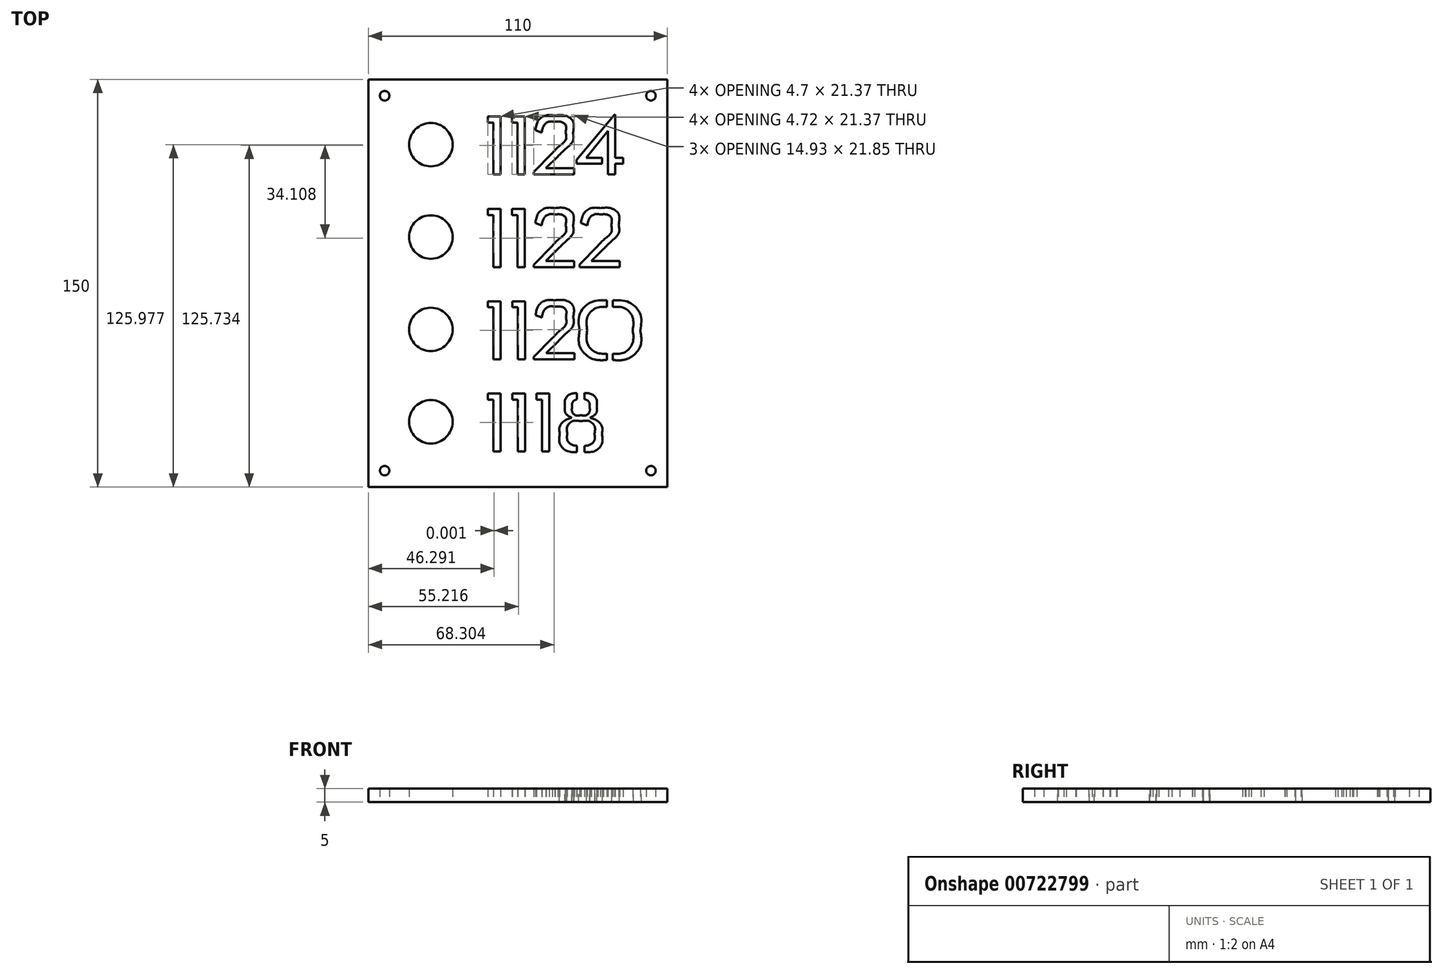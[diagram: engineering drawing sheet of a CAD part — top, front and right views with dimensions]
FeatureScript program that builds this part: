
annotation { "Feature Type Name" : "Feature", "Feature Type Description" : "" }
export const myFeature = defineFeature(function(context is Context, id is Id, definition is map)
    precondition{}
    {
        {
            var Q0;
            Q0=qCreatedBy(makeId("Top.planeOp"),FACE);
            var sketch = newSketch(context, id + "F0", { "sketchPlane" : qUnion([Q0])});
            skLineSegment(sketch, "E0.bottom", {"start": v(-57.93, 74.31) * mm, "end": v(52.07, 74.31) * mm});
            skLineSegment(sketch, "E0.top", {"start": v(-57.93, -75.69) * mm, "end": v(52.07, -75.69) * mm});
            skLineSegment(sketch, "E0.left", {"start": v(-57.93, 74.31) * mm, "end": v(-57.93, -75.69) * mm});
            skLineSegment(sketch, "E0.right", {"start": v(52.07, 74.31) * mm, "end": v(52.07, -75.69) * mm});
            skCircle(sketch, "E1", {"center": v(-51.93, 68.31) * mm, "radius": 1.75 * mm});
            skLineSegment(sketch, "E2.bottom", {"start": v(-57.93, 74.31) * mm, "end": v(-41.03, 74.31) * mm});
            skLineSegment(sketch, "E2.left", {"start": v(-57.93, 74.31) * mm, "end": v(-57.93, 53.12) * mm});
            skLineSegment(sketch, "E3.left", {"start": v(52.07, 74.31) * mm, "end": v(52.07, 53.12) * mm});
            skCircle(sketch, "E4", {"center": v(46.07, 68.31) * mm, "radius": 1.75 * mm});
            skCircle(sketch, "E5", {"center": v(-51.93, -69.69) * mm, "radius": 1.75 * mm});
            skCircle(sketch, "E6", {"center": v(46.07, -69.69) * mm, "radius": 1.75 * mm});
            skCircle(sketch, "E7", {"center": v(-34.93, 50.31) * mm, "radius": 8 * mm});
            skCircle(sketch, "E8", {"center": v(-34.93, 16.31) * mm, "radius": 8 * mm});
            skCircle(sketch, "E9", {"center": v(-34.93, -17.69) * mm, "radius": 8 * mm});
            skCircle(sketch, "E10", {"center": v(-34.93, -51.69) * mm, "radius": 8 * mm});
            skLineSegment(sketch, "E11", {"start": v(-13.99, 24.37) * mm, "end": v(-11.95, 24.37) * mm});
            skLineSegment(sketch, "E12", {"start": v(-11.95, 24.37) * mm, "end": v(-11.95, 5.25) * mm});
            skLineSegment(sketch, "E13", {"start": v(-11.95, 5.25) * mm, "end": v(-9.29, 5.25) * mm});
            skLineSegment(sketch, "E14", {"start": v(-9.29, 5.25) * mm, "end": v(-9.29, 26.62) * mm});
            skLineSegment(sketch, "E15", {"start": v(-9.29, 26.62) * mm, "end": v(-13.99, 26.62) * mm});
            skLineSegment(sketch, "E16", {"start": v(-13.99, 26.62) * mm, "end": v(-13.99, 24.37) * mm});
            skLineSegment(sketch, "E17", {"start": v(-5.07, 24.37) * mm, "end": v(-3.02, 24.37) * mm});
            skLineSegment(sketch, "E18", {"start": v(-3.02, 24.37) * mm, "end": v(-3.02, 5.25) * mm});
            skLineSegment(sketch, "E19", {"start": v(-3.02, 5.25) * mm, "end": v(-0.35, 5.25) * mm});
            skLineSegment(sketch, "E20", {"start": v(-0.35, 5.25) * mm, "end": v(-0.35, 26.62) * mm});
            skLineSegment(sketch, "E21", {"start": v(-0.35, 26.62) * mm, "end": v(-5.07, 26.62) * mm});
            skLineSegment(sketch, "E22", {"start": v(-5.07, 26.62) * mm, "end": v(-5.07, 24.37) * mm});
            skLineSegment(sketch, "E23", {"start": v(24.17, 7.5) * mm, "end": v(28.58, 11.87) * mm});
            skLineSegment(sketch, "E24", {"start": v(20.3, 21.5) * mm, "end": v(22.63, 20.62) * mm});
            skLineSegment(sketch, "E25", {"start": v(26.54, 13.08) * mm, "end": v(19.84, 6.27) * mm});
            skLineSegment(sketch, "E26", {"start": v(19.84, 6.27) * mm, "end": v(19.84, 5.25) * mm});
            skLineSegment(sketch, "E27", {"start": v(19.84, 5.25) * mm, "end": v(34.62, 5.25) * mm});
            skLineSegment(sketch, "E28", {"start": v(34.62, 5.25) * mm, "end": v(34.62, 7.5) * mm});
            skLineSegment(sketch, "E29", {"start": v(34.62, 7.5) * mm, "end": v(24.17, 7.5) * mm});
            skLineSegment(sketch, "E30", {"start": v(3.51, 21.5) * mm, "end": v(5.84, 20.62) * mm});
            skLineSegment(sketch, "E31", {"start": v(9.76, 13.08) * mm, "end": v(2.9, 6.12) * mm});
            skLineSegment(sketch, "E32", {"start": v(2.9, 6.12) * mm, "end": v(2.9, 5.25) * mm});
            skLineSegment(sketch, "E33", {"start": v(2.9, 5.25) * mm, "end": v(17.84, 5.25) * mm});
            skLineSegment(sketch, "E34", {"start": v(17.84, 5.25) * mm, "end": v(17.84, 7.5) * mm});
            skLineSegment(sketch, "E35", {"start": v(17.84, 7.5) * mm, "end": v(7.39, 7.5) * mm});
            skLineSegment(sketch, "E36", {"start": v(7.39, 7.5) * mm, "end": v(11.8, 11.88) * mm});
            skLineSegment(sketch, "E37", {"start": v(-13.9, -9.56) * mm, "end": v(-11.87, -9.56) * mm});
            skLineSegment(sketch, "E38", {"start": v(-11.87, -9.56) * mm, "end": v(-11.87, -28.68) * mm});
            skLineSegment(sketch, "E39", {"start": v(-11.87, -28.68) * mm, "end": v(-9.2, -28.68) * mm});
            skLineSegment(sketch, "E40", {"start": v(-9.2, -28.68) * mm, "end": v(-9.2, -7.31) * mm});
            skLineSegment(sketch, "E41", {"start": v(-9.2, -7.31) * mm, "end": v(-13.9, -7.31) * mm});
            skLineSegment(sketch, "E42", {"start": v(-13.9, -7.31) * mm, "end": v(-13.9, -9.56) * mm});
            skLineSegment(sketch, "E43", {"start": v(3.6, -12.44) * mm, "end": v(5.93, -13.31) * mm});
            skLineSegment(sketch, "E44", {"start": v(9.84, -20.85) * mm, "end": v(3, -27.81) * mm});
            skLineSegment(sketch, "E45", {"start": v(3, -27.81) * mm, "end": v(3, -28.68) * mm});
            skLineSegment(sketch, "E46", {"start": v(3, -28.68) * mm, "end": v(17.92, -28.68) * mm});
            skLineSegment(sketch, "E47", {"start": v(17.92, -28.68) * mm, "end": v(17.92, -26.43) * mm});
            skLineSegment(sketch, "E48", {"start": v(17.92, -26.43) * mm, "end": v(7.47, -26.43) * mm});
            skLineSegment(sketch, "E49", {"start": v(7.47, -26.43) * mm, "end": v(11.88, -22.06) * mm});
            skLineSegment(sketch, "E50", {"start": v(-4.99, -9.56) * mm, "end": v(-2.94, -9.56) * mm});
            skLineSegment(sketch, "E51", {"start": v(-2.94, -9.56) * mm, "end": v(-2.94, -28.68) * mm});
            skLineSegment(sketch, "E52", {"start": v(-2.94, -28.68) * mm, "end": v(-0.27, -28.68) * mm});
            skLineSegment(sketch, "E53", {"start": v(-0.27, -28.68) * mm, "end": v(-0.27, -7.31) * mm});
            skLineSegment(sketch, "E54", {"start": v(-0.27, -7.31) * mm, "end": v(-4.99, -7.31) * mm});
            skLineSegment(sketch, "E55", {"start": v(-4.99, -7.31) * mm, "end": v(-4.99, -9.56) * mm});
            skLineSegment(sketch, "E56", {"start": v(32.01, -7.03) * mm, "end": v(32.01, -9.38) * mm});
            skLineSegment(sketch, "E57", {"start": v(32.01, -26.62) * mm, "end": v(32.01, -28.96) * mm});
            skLineSegment(sketch, "E58", {"start": v(29.82, -9.4) * mm, "end": v(29.82, -7.04) * mm});
            skLineSegment(sketch, "E59", {"start": v(29.82, -28.96) * mm, "end": v(29.82, -26.6) * mm});
            skLineSegment(sketch, "E60", {"start": v(-13.99, 58.48) * mm, "end": v(-11.95, 58.48) * mm});
            skLineSegment(sketch, "E61", {"start": v(-11.95, 58.48) * mm, "end": v(-11.95, 39.36) * mm});
            skLineSegment(sketch, "E62", {"start": v(-11.95, 39.36) * mm, "end": v(-9.29, 39.36) * mm});
            skLineSegment(sketch, "E63", {"start": v(-9.29, 39.36) * mm, "end": v(-9.29, 60.73) * mm});
            skLineSegment(sketch, "E64", {"start": v(-9.29, 60.73) * mm, "end": v(-13.99, 60.73) * mm});
            skLineSegment(sketch, "E65", {"start": v(-13.99, 60.73) * mm, "end": v(-13.99, 58.48) * mm});
            skLineSegment(sketch, "E66", {"start": v(-5.07, 58.48) * mm, "end": v(-3.02, 58.48) * mm});
            skLineSegment(sketch, "E67", {"start": v(-3.02, 58.48) * mm, "end": v(-3.02, 39.36) * mm});
            skLineSegment(sketch, "E68", {"start": v(-3.02, 39.36) * mm, "end": v(-0.36, 39.36) * mm});
            skLineSegment(sketch, "E69", {"start": v(-0.36, 39.36) * mm, "end": v(-0.36, 60.73) * mm});
            skLineSegment(sketch, "E70", {"start": v(-0.36, 60.73) * mm, "end": v(-5.07, 60.73) * mm});
            skLineSegment(sketch, "E71", {"start": v(-5.07, 60.73) * mm, "end": v(-5.07, 58.48) * mm});
            skLineSegment(sketch, "E72", {"start": v(32.92, 45.52) * mm, "end": v(32.92, 61.35) * mm});
            skLineSegment(sketch, "E73", {"start": v(32.92, 61.35) * mm, "end": v(32.7, 61.35) * mm});
            skLineSegment(sketch, "E74", {"start": v(32.7, 61.35) * mm, "end": v(18.71, 44.73) * mm});
            skLineSegment(sketch, "E75", {"start": v(18.71, 44.73) * mm, "end": v(18.71, 43.32) * mm});
            skLineSegment(sketch, "E76", {"start": v(18.71, 43.32) * mm, "end": v(28.13, 43.32) * mm});
            skLineSegment(sketch, "E77", {"start": v(28.13, 43.32) * mm, "end": v(28.13, 45.52) * mm});
            skLineSegment(sketch, "E78", {"start": v(28.13, 45.52) * mm, "end": v(22.3, 45.52) * mm});
            skLineSegment(sketch, "E79", {"start": v(22.3, 45.52) * mm, "end": v(30.3, 55.31) * mm});
            skLineSegment(sketch, "E80", {"start": v(30.3, 55.31) * mm, "end": v(30.3, 39.36) * mm});
            skLineSegment(sketch, "E81", {"start": v(30.3, 39.36) * mm, "end": v(32.92, 39.36) * mm});
            skLineSegment(sketch, "E82", {"start": v(32.92, 39.36) * mm, "end": v(32.92, 43.32) * mm});
            skLineSegment(sketch, "E83", {"start": v(32.92, 43.32) * mm, "end": v(35.8, 43.32) * mm});
            skLineSegment(sketch, "E84", {"start": v(35.8, 43.32) * mm, "end": v(35.8, 45.52) * mm});
            skLineSegment(sketch, "E85", {"start": v(35.8, 45.52) * mm, "end": v(32.92, 45.52) * mm});
            skLineSegment(sketch, "E86", {"start": v(3.51, 55.6) * mm, "end": v(5.84, 54.73) * mm});
            skLineSegment(sketch, "E87", {"start": v(9.76, 47.2) * mm, "end": v(2.9, 40.23) * mm});
            skLineSegment(sketch, "E88", {"start": v(2.9, 40.23) * mm, "end": v(2.9, 39.36) * mm});
            skLineSegment(sketch, "E89", {"start": v(2.9, 39.36) * mm, "end": v(17.84, 39.36) * mm});
            skLineSegment(sketch, "E90", {"start": v(17.84, 39.36) * mm, "end": v(17.84, 41.6) * mm});
            skLineSegment(sketch, "E91", {"start": v(17.84, 41.6) * mm, "end": v(7.38, 41.6) * mm});
            skLineSegment(sketch, "E92", {"start": v(7.38, 41.6) * mm, "end": v(11.8, 45.98) * mm});
            skLineSegment(sketch, "E93", {"start": v(-13.92, -43.54) * mm, "end": v(-11.89, -43.54) * mm});
            skLineSegment(sketch, "E94", {"start": v(-11.89, -43.54) * mm, "end": v(-11.89, -62.66) * mm});
            skLineSegment(sketch, "E95", {"start": v(-11.89, -62.66) * mm, "end": v(-9.22, -62.66) * mm});
            skLineSegment(sketch, "E96", {"start": v(-9.22, -62.66) * mm, "end": v(-9.22, -41.29) * mm});
            skLineSegment(sketch, "E97", {"start": v(-9.22, -41.29) * mm, "end": v(-13.92, -41.29) * mm});
            skLineSegment(sketch, "E98", {"start": v(-13.92, -41.29) * mm, "end": v(-13.92, -43.54) * mm});
            skLineSegment(sketch, "E99", {"start": v(-5, -43.54) * mm, "end": v(-2.95, -43.54) * mm});
            skLineSegment(sketch, "E100", {"start": v(-2.95, -43.54) * mm, "end": v(-2.95, -62.66) * mm});
            skLineSegment(sketch, "E101", {"start": v(-2.95, -62.66) * mm, "end": v(-0.29, -62.66) * mm});
            skLineSegment(sketch, "E102", {"start": v(-0.29, -62.66) * mm, "end": v(-0.29, -41.29) * mm});
            skLineSegment(sketch, "E103", {"start": v(-0.29, -41.29) * mm, "end": v(-5, -41.29) * mm});
            skLineSegment(sketch, "E104", {"start": v(-5, -41.29) * mm, "end": v(-5, -43.54) * mm});
            skLineSegment(sketch, "E105", {"start": v(21.62, -41.08) * mm, "end": v(21.62, -43.4) * mm});
            skLineSegment(sketch, "E106", {"start": v(18.86, -43.44) * mm, "end": v(18.86, -41.1) * mm});
            skLineSegment(sketch, "E107", {"start": v(18.86, -62.89) * mm, "end": v(18.86, -60.53) * mm});
            skLineSegment(sketch, "E108", {"start": v(21.62, -60.55) * mm, "end": v(21.62, -62.9) * mm});
            skLineSegment(sketch, "E109", {"start": v(3.91, -43.54) * mm, "end": v(5.98, -43.54) * mm});
            skLineSegment(sketch, "E110", {"start": v(5.98, -43.54) * mm, "end": v(5.98, -62.66) * mm});
            skLineSegment(sketch, "E111", {"start": v(5.98, -62.66) * mm, "end": v(8.65, -62.66) * mm});
            skLineSegment(sketch, "E112", {"start": v(8.65, -62.66) * mm, "end": v(8.65, -41.29) * mm});
            skLineSegment(sketch, "E113", {"start": v(8.65, -41.29) * mm, "end": v(3.91, -41.29) * mm});
            skLineSegment(sketch, "E114", {"start": v(3.91, -41.29) * mm, "end": v(3.91, -43.54) * mm});
            skFitSpline(sketch, "E115", {"points": [v(28.58, 11.87) * mm, v(31.3, 14.54) * mm, v(34.16, 17.66) * mm, v(34.16, 20.75) * mm]});
            skFitSpline(sketch, "E116", {"points": [v(34.16, 20.75) * mm, v(34.16, 24.79) * mm, v(31.17, 26.95) * mm, v(27.46, 26.95) * mm]});
            skFitSpline(sketch, "E117", {"points": [v(27.46, 26.95) * mm, v(24.13, 26.95) * mm, v(21.38, 25) * mm, v(20.3, 21.5) * mm]});
            skFitSpline(sketch, "E118", {"points": [v(22.63, 20.62) * mm, v(23.33, 23.04) * mm, v(25.13, 24.62) * mm, v(27.46, 24.62) * mm]});
            skFitSpline(sketch, "E119", {"points": [v(27.46, 24.62) * mm, v(29.67, 24.62) * mm, v(31.46, 23.45) * mm, v(31.46, 20.75) * mm]});
            skFitSpline(sketch, "E120", {"points": [v(31.46, 20.75) * mm, v(31.46, 18) * mm, v(29, 15.58) * mm, v(26.54, 13.08) * mm]});
            skFitSpline(sketch, "E121", {"points": [v(11.8, 11.88) * mm, v(14.5, 14.54) * mm, v(17.38, 17.66) * mm, v(17.38, 20.75) * mm]});
            skFitSpline(sketch, "E122", {"points": [v(17.38, 20.75) * mm, v(17.38, 24.79) * mm, v(14.38, 26.95) * mm, v(10.68, 26.95) * mm]});
            skFitSpline(sketch, "E123", {"points": [v(10.68, 26.95) * mm, v(7.34, 26.95) * mm, v(4.6, 25) * mm, v(3.51, 21.5) * mm]});
            skFitSpline(sketch, "E124", {"points": [v(5.84, 20.62) * mm, v(6.55, 23.04) * mm, v(8.34, 24.62) * mm, v(10.68, 24.62) * mm]});
            skFitSpline(sketch, "E125", {"points": [v(10.68, 24.62) * mm, v(12.88, 24.62) * mm, v(14.67, 23.45) * mm, v(14.67, 20.75) * mm]});
            skFitSpline(sketch, "E126", {"points": [v(14.67, 20.75) * mm, v(14.67, 18) * mm, v(12.22, 15.58) * mm, v(9.76, 13.08) * mm]});
            skFitSpline(sketch, "E127", {"points": [v(11.88, -22.06) * mm, v(14.6, -19.4) * mm, v(17.47, -16.27) * mm, v(17.47, -13.19) * mm]});
            skFitSpline(sketch, "E128", {"points": [v(17.47, -13.19) * mm, v(17.47, -9.15) * mm, v(14.47, -6.98) * mm, v(10.76, -6.98) * mm]});
            skFitSpline(sketch, "E129", {"points": [v(10.76, -6.98) * mm, v(7.43, -6.98) * mm, v(4.68, -8.94) * mm, v(3.6, -12.44) * mm]});
            skFitSpline(sketch, "E130", {"points": [v(5.93, -13.31) * mm, v(6.64, -10.9) * mm, v(8.43, -9.31) * mm, v(10.76, -9.31) * mm]});
            skFitSpline(sketch, "E131", {"points": [v(10.76, -9.31) * mm, v(12.97, -9.31) * mm, v(14.76, -10.48) * mm, v(14.76, -13.19) * mm]});
            skFitSpline(sketch, "E132", {"points": [v(14.76, -13.19) * mm, v(14.76, -15.94) * mm, v(12.3, -18.35) * mm, v(9.84, -20.85) * mm]});
            skFitSpline(sketch, "E133", {"points": [v(32.01, -9.38) * mm, v(36.3, -9.86) * mm, v(39.33, -13.27) * mm, v(39.33, -17.98) * mm]});
            skFitSpline(sketch, "E134", {"points": [v(39.33, -17.98) * mm, v(39.33, -22.64) * mm, v(36.3, -26.12) * mm, v(32.01, -26.62) * mm]});
            skFitSpline(sketch, "E135", {"points": [v(32.01, -28.96) * mm, v(37.62, -28.45) * mm, v(42.12, -23.9) * mm, v(42.12, -17.98) * mm]});
            skFitSpline(sketch, "E136", {"points": [v(42.12, -17.98) * mm, v(42.12, -12.01) * mm, v(37.62, -7.53) * mm, v(32.01, -7.03) * mm]});
            skFitSpline(sketch, "E137", {"points": [v(29.82, -26.6) * mm, v(25.62, -26.07) * mm, v(22.63, -22.6) * mm, v(22.63, -17.98) * mm]});
            skFitSpline(sketch, "E138", {"points": [v(22.63, -17.98) * mm, v(22.63, -13.3) * mm, v(25.62, -9.91) * mm, v(29.82, -9.4) * mm]});
            skFitSpline(sketch, "E139", {"points": [v(29.82, -7.04) * mm, v(24.3, -7.58) * mm, v(19.84, -12.05) * mm, v(19.84, -17.98) * mm]});
            skFitSpline(sketch, "E140", {"points": [v(19.84, -17.98) * mm, v(19.84, -23.87) * mm, v(24.3, -28.4) * mm, v(29.82, -28.96) * mm]});
            skFitSpline(sketch, "E141", {"points": [v(11.8, 45.98) * mm, v(14.5, 48.65) * mm, v(17.38, 51.77) * mm, v(17.38, 54.85) * mm]});
            skFitSpline(sketch, "E142", {"points": [v(17.38, 54.85) * mm, v(17.38, 58.9) * mm, v(14.38, 61.06) * mm, v(10.68, 61.06) * mm]});
            skFitSpline(sketch, "E143", {"points": [v(10.68, 61.06) * mm, v(7.34, 61.06) * mm, v(4.6, 59.1) * mm, v(3.51, 55.6) * mm]});
            skFitSpline(sketch, "E144", {"points": [v(5.84, 54.73) * mm, v(6.55, 57.15) * mm, v(8.34, 58.73) * mm, v(10.68, 58.73) * mm]});
            skFitSpline(sketch, "E145", {"points": [v(10.68, 58.73) * mm, v(12.88, 58.73) * mm, v(14.67, 57.56) * mm, v(14.67, 54.85) * mm]});
            skFitSpline(sketch, "E146", {"points": [v(14.67, 54.85) * mm, v(14.67, 52.1) * mm, v(12.22, 49.69) * mm, v(9.76, 47.2) * mm]});
            skFitSpline(sketch, "E147", {"points": [v(23.6, -50.24) * mm, v(25.06, -49.41) * mm, v(26.1, -48.04) * mm, v(26.1, -46.12) * mm]});
            skFitSpline(sketch, "E148", {"points": [v(26.1, -46.12) * mm, v(26.1, -43.7) * mm, v(24.38, -41.6) * mm, v(21.62, -41.08) * mm]});
            skFitSpline(sketch, "E149", {"points": [v(21.62, -43.4) * mm, v(22.77, -43.85) * mm, v(23.48, -44.89) * mm, v(23.48, -46.24) * mm]});
            skFitSpline(sketch, "E150", {"points": [v(23.48, -46.24) * mm, v(23.48, -48.04) * mm, v(22.23, -49.29) * mm, v(20.27, -49.29) * mm]});
            skFitSpline(sketch, "E151", {"points": [v(20.27, -49.29) * mm, v(18.35, -49.29) * mm, v(17.06, -48.04) * mm, v(17.06, -46.24) * mm]});
            skFitSpline(sketch, "E152", {"points": [v(17.06, -46.24) * mm, v(17.06, -44.92) * mm, v(17.76, -43.9) * mm, v(18.86, -43.44) * mm]});
            skFitSpline(sketch, "E153", {"points": [v(18.86, -41.1) * mm, v(16.14, -41.63) * mm, v(14.44, -43.72) * mm, v(14.44, -46.12) * mm]});
            skFitSpline(sketch, "E154", {"points": [v(14.44, -46.12) * mm, v(14.44, -48.04) * mm, v(15.48, -49.41) * mm, v(16.94, -50.24) * mm]});
            skFitSpline(sketch, "E155", {"points": [v(16.94, -50.24) * mm, v(14.31, -51.24) * mm, v(12.52, -53.4) * mm, v(12.52, -56.24) * mm]});
            skFitSpline(sketch, "E156", {"points": [v(12.52, -56.24) * mm, v(12.52, -59.67) * mm, v(15.03, -62.36) * mm, v(18.86, -62.89) * mm]});
            skFitSpline(sketch, "E157", {"points": [v(18.86, -60.53) * mm, v(16.69, -60.01) * mm, v(15.27, -58.29) * mm, v(15.27, -56.03) * mm]});
            skFitSpline(sketch, "E158", {"points": [v(15.27, -56.03) * mm, v(15.27, -53.37) * mm, v(17.23, -51.45) * mm, v(20.27, -51.45) * mm]});
            skFitSpline(sketch, "E159", {"points": [v(20.27, -51.45) * mm, v(23.35, -51.45) * mm, v(25.3, -53.37) * mm, v(25.3, -56.03) * mm]});
            skFitSpline(sketch, "E160", {"points": [v(25.3, -56.03) * mm, v(25.3, -58.3) * mm, v(23.86, -60.05) * mm, v(21.62, -60.55) * mm]});
            skFitSpline(sketch, "E161", {"points": [v(21.62, -62.9) * mm, v(25.52, -62.39) * mm, v(28.02, -59.69) * mm, v(28.02, -56.24) * mm]});
            skFitSpline(sketch, "E162", {"points": [v(28.02, -56.24) * mm, v(28.02, -53.4) * mm, v(26.22, -51.24) * mm, v(23.6, -50.24) * mm]});
            skLineSegment(sketch, "E163", {"start": v(-57.93, 39.31) * mm, "end": v(52.07, 39.31) * mm});
            skLineSegment(sketch, "E164", {"start": v(-57.93, 5.31) * mm, "end": v(52.07, 5.31) * mm});
            skLineSegment(sketch, "E165", {"start": v(-57.93, -28.69) * mm, "end": v(52.07, -28.69) * mm});
            skSolve(sketch);
        }
        {
            var Q0;
            Q0 = qSketchRegion(id + "F0", true);
            extrude(context, id + "F1", {"entities" : qUnion([Q0]), "depth" : 5 * mm, "offsetDistance" : 25 * mm});
        }
    });
